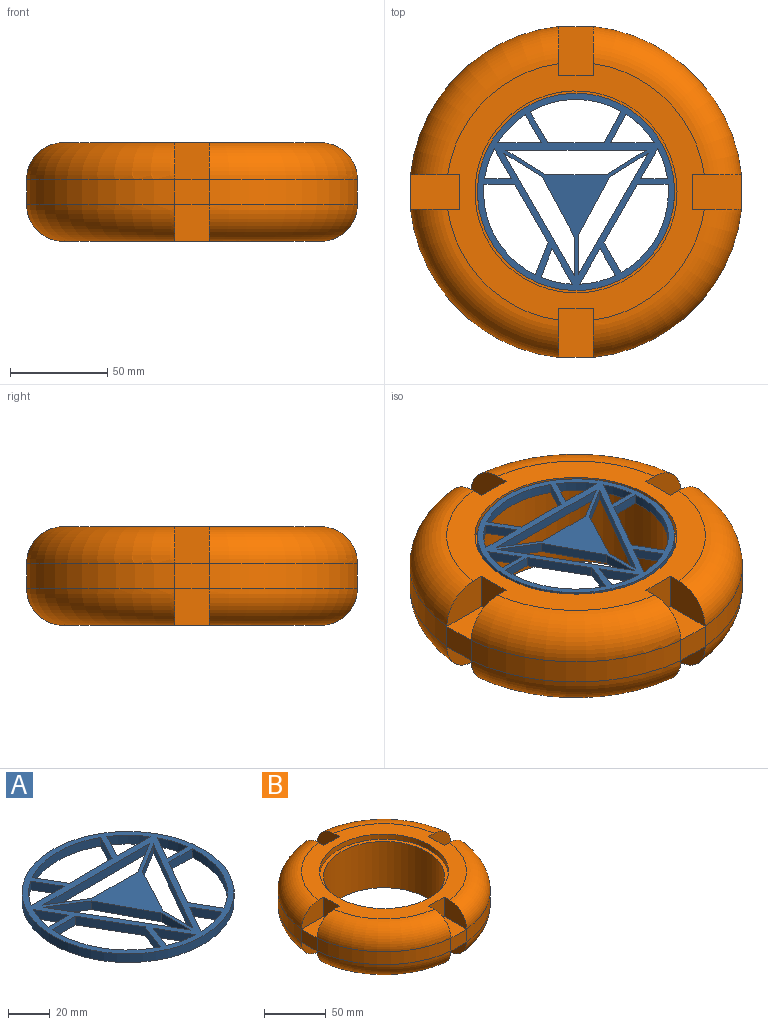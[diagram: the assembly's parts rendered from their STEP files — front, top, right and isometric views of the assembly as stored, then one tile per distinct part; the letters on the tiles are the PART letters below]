
ASSEMBLY  parts=2 mates=1
PART A: 45 faces, bbox 101.6x101.6x5.1 mm
  f0: plane 15.9x9.18mm, normal (0.87,0.5,0), area 93.3mm2, adj f1,f30,f43,f44
  f1: cylinder r=47.62mm len=46.89mm, axis (0,0,-1), area 249mm2, adj f0,f2,f43,f44
  f2: plane 16.2x8.64mm, normal (-0.88,0.47,0), area 93.3mm2, adj f1,f30,f43,f44
  f3: plane 22.36x5.08mm, normal (0,1,0), area 113.6mm2, adj f4,f31,f43,f44
  f4: plane 14.67x7.82mm, normal (0.88,-0.47,0), area 84.4mm2, adj f3,f31,f43,f44
  f5: plane 15.58x8.99mm, normal (0.87,0.5,0), area 91.4mm2, adj f6,f32,f43,f44
  f6: plane 29.95x17.29mm, normal (0.87,-0.5,0), area 175.7mm2, adj f5,f7,f43,f44
  f7: plane 15.8x5.08mm, normal (0,-1,0), area 80.3mm2, adj f6,f32,f43,f44
  f8: cylinder r=47.62mm len=16.12mm, axis (0,0,-1), area 84.2mm2, adj f9,f33,f43,f44
  f9: plane 14.79x5.57mm, normal (0.94,-0.35,0), area 80.3mm2, adj f8,f33,f43,f44
  f10: plane 30.93x16.49mm, normal (-0.88,-0.47,0), area 178mm2, adj f11,f34,f43,f44
  f11: plane 19.79x5.08mm, normal (-1,0,0), area 100.5mm2, adj f10,f12,f43,f44
  f12: plane 63.03x36.39mm, normal (0.87,0.5,0), area 369.7mm2, adj f11,f34,f43,f44
  f13: plane 30.31x16.16mm, normal (0.88,-0.47,0), area 174.5mm2, adj f14,f35,f43,f44
  f14: plane 19.9x12.32mm, normal (0.53,-0.85,0), area 118.9mm2, adj f13,f15,f43,f44
  f15: plane 62.46x36.06mm, normal (-0.87,0.5,0), area 366.4mm2, adj f14,f35,f43,f44
  f16: plane 31.25x5.08mm, normal (0,1,0), area 158.7mm2, adj f17,f36,f43,f44
  f17: plane 20.52x12.7mm, normal (0.53,0.85,0), area 122.6mm2, adj f16,f18,f43,f44
  f18: plane 72.28x5.08mm, normal (0,-1,0), area 367.2mm2, adj f17,f36,f43,f44
  f19: cylinder r=47.62mm len=14.36mm, axis (0,0,-1), area 102.9mm2, adj f20,f37,f43,f44
  f20: plane 14.36x8.29mm, normal (-0.87,-0.5,0), area 84.2mm2, adj f19,f37,f43,f44
  f21: cylinder r=47.62mm len=18.49mm, axis (0,0,-1), area 97.4mm2, adj f22,f38,f43,f44
  f22: plane 18.28x10.55mm, normal (0.87,-0.5,0), area 107.2mm2, adj f21,f38,f43,f44
  f23: cylinder r=47.62mm len=15.4mm, axis (0,0,-1), area 82.6mm2, adj f24,f39,f43,f44
  f24: plane 15.4x8.89mm, normal (-0.87,-0.5,0), area 90.3mm2, adj f23,f39,f43,f44
  f25: plane 29.95x17.29mm, normal (-0.87,-0.5,0), area 175.7mm2, adj f26,f40,f43,f44
  f26: plane 16.83x6.61mm, normal (-0.93,0.37,0), area 91.8mm2, adj f25,f27,f43,f44
  f27: cylinder r=47.62mm len=46.79mm, axis (0,0,-1), area 290.2mm2, adj f26,f40,f43,f44
  f28: plane 13.89x5.08mm, normal (0,1,0), area 70.6mm2, adj f29,f41,f43,f44
  f29: plane 15.4x8.89mm, normal (0.87,-0.5,0), area 90.3mm2, adj f28,f41,f43,f44
  f30: plane 29.07x5.08mm, normal (0,1,0), area 147.7mm2, adj f0,f2,f43,f44
  f31: cylinder r=47.62mm len=14.67mm, axis (0,0,-1), area 105.8mm2, adj f3,f4,f43,f44
  f32: cylinder r=47.62mm len=45.53mm, axis (0,0,-1), area 276.5mm2, adj f5,f7,f43,f44
  f33: plane 18.28x10.55mm, normal (-0.87,-0.5,0), area 107.2mm2, adj f8,f9,f43,f44
  f34: plane 19.9x12.32mm, normal (-0.53,-0.85,0), area 118.9mm2, adj f10,f12,f43,f44
  f35: plane 19.83x5.08mm, normal (1,0,0), area 100.7mm2, adj f13,f15,f43,f44
  f36: plane 20.52x12.7mm, normal (-0.53,0.85,0), area 122.6mm2, adj f16,f18,f43,f44
  f37: plane 22.36x5.08mm, normal (0,1,0), area 113.6mm2, adj f19,f20,f43,f44
  f38: plane 13.75x7.94mm, normal (-0.87,-0.5,0), area 80.6mm2, adj f21,f22,f43,f44
  f39: plane 13.89x5.08mm, normal (0,1,0), area 70.6mm2, adj f23,f24,f43,f44
  f40: plane 15.8x5.08mm, normal (0,-1,0), area 80.3mm2, adj f25,f27,f43,f44
  f41: cylinder r=47.62mm len=15.4mm, axis (0,0,-1), area 82.6mm2, adj f28,f29,f43,f44
  f42: cylinder r=50.8mm len=101.6mm, axis (0,0,-1), area 1621.5mm2, adj f43,f44
  f43: plane 101.6x101.6mm, normal (0,0,1), area 2830.3mm2, adj f0,f1,f2,f3,f4,f5,f6,f7
  f44: plane 101.6x101.6mm, normal (0,0,-1), area 2830.3mm2, adj f0,f1,f2,f3,f4,f5,f6,f7
PART B: 53 faces, bbox 184.6x184.6x50.8 mm
  f0: plane 25.4x19.05mm, normal (1,0,0), area 405.5mm2, adj f19,f30,f32,f49
  f1: plane 19.05x17.78mm, normal (0,-1,0), area 338.7mm2, adj f18,f20,f29,f50
  f2: plane 25.4x19.05mm, normal (-1,0,0), area 405.5mm2, adj f19,f30,f31,f49
  f3: plane 25.4x19.05mm, normal (0,-1,0), area 405.5mm2, adj f15,f30,f34,f46
  f4: plane 19.05x17.78mm, normal (-1,0,0), area 338.7mm2, adj f14,f16,f29,f47
  f5: plane 25.4x19.05mm, normal (0,1,0), area 405.5mm2, adj f15,f30,f32,f46
  f6: plane 25.4x19.05mm, normal (1,0,0), area 405.5mm2, adj f8,f30,f34,f43
  f7: plane 25.4x19.05mm, normal (-1,0,0), area 405.5mm2, adj f8,f30,f33,f43
  f8: plane 19.05x17.78mm, normal (0,1,0), area 338.7mm2, adj f6,f7,f30,f43
  f9: plane 25.4x19.05mm, normal (0,1,0), area 405.5mm2, adj f10,f30,f31,f40
  f10: plane 19.05x17.78mm, normal (1,0,0), area 338.7mm2, adj f9,f11,f30,f40
  f11: plane 25.4x19.05mm, normal (0,-1,0), area 405.5mm2, adj f10,f30,f33,f40
  f12: plane 25.4x19.05mm, normal (1,0,0), area 405.5mm2, adj f28,f29,f38,f44
  f13: cylinder r=85.72mm len=76.37mm, axis (0,0,-1), area 1483.9mm2, adj f34,f38,f42,f45
  f14: plane 25.4x19.05mm, normal (0,-1,0), area 405.5mm2, adj f4,f29,f38,f47
  f15: plane 19.05x17.78mm, normal (-1,0,0), area 338.7mm2, adj f3,f5,f30,f46
  f16: plane 25.4x19.05mm, normal (0,1,0), area 405.5mm2, adj f4,f29,f36,f47
  f17: cylinder r=85.72mm len=76.37mm, axis (0,0,-1), area 1483.9mm2, adj f32,f36,f45,f48
  f18: plane 25.4x19.05mm, normal (1,0,0), area 405.5mm2, adj f1,f29,f36,f50
  f19: plane 19.05x17.78mm, normal (0,-1,0), area 338.7mm2, adj f0,f2,f30,f49
  f20: plane 25.4x19.05mm, normal (-1,0,0), area 405.5mm2, adj f1,f29,f35,f50
  f21: cylinder r=85.72mm len=76.37mm, axis (0,0,-1), area 1483.9mm2, adj f31,f35,f39,f48
  f22: plane 25.4x19.05mm, normal (0,1,0), area 405.5mm2, adj f23,f29,f35,f41
  f23: plane 19.05x17.78mm, normal (1,0,0), area 338.7mm2, adj f22,f24,f29,f41
  f24: plane 25.4x19.05mm, normal (0,-1,0), area 405.5mm2, adj f23,f29,f37,f41
  f25: cylinder r=85.72mm len=76.37mm, axis (0,0,-1), area 1483.9mm2, adj f33,f37,f39,f42
  f26: plane 25.4x19.05mm, normal (-1,0,0), area 405.5mm2, adj f28,f29,f37,f44
  f27: cylinder r=52.07mm len=104.14mm, axis (0,0,-1), area 1662mm2, adj f29,f52
  f28: plane 19.05x17.78mm, normal (0,1,0), area 338.7mm2, adj f12,f26,f29,f44
  f29: plane 132.16x132.16mm, normal (0,0,1), area 4978mm2, adj f1,f4,f12,f14,f16,f18,f20,f22
  f30: plane 132.16x132.16mm, normal (0,0,-1), area 5985.1mm2, adj f0,f2,f3,f5,f6,f7,f8,f9
  f31: torus R=66.67mm, axis (0,0,1), area 3170.9mm2, adj f2,f9,f21,f30
  f32: torus R=66.67mm, axis (0,0,1), area 3170.9mm2, adj f0,f5,f17,f30
  f33: torus R=66.67mm, axis (0,0,1), area 3170.9mm2, adj f7,f11,f25,f30
  f34: torus R=66.67mm, axis (0,0,1), area 3170.9mm2, adj f3,f6,f13,f30
  f35: torus R=66.67mm, axis (0,0,1), area 3170.8mm2, adj f20,f21,f22,f29
  f36: torus R=66.67mm, axis (0,0,1), area 3170.8mm2, adj f16,f17,f18,f29
  f37: torus R=66.67mm, axis (0,0,1), area 3170.8mm2, adj f24,f25,f26,f29
  f38: torus R=66.67mm, axis (0,0,1), area 3170.8mm2, adj f12,f13,f14,f29
  f39: plane 17.78x12.7mm, normal (1,0,0), area 225.8mm2, adj f21,f25,f40,f41
  f40: plane 25.4x17.78mm, normal (0,0,-1), area 451.6mm2, adj f9,f10,f11,f39
  f41: plane 25.4x17.78mm, normal (0,0,1), area 451.6mm2, adj f22,f23,f24,f39
  f42: plane 17.78x12.7mm, normal (0,1,0), area 225.8mm2, adj f13,f25,f43,f44
  f43: plane 25.4x17.78mm, normal (0,0,-1), area 451.6mm2, adj f6,f7,f8,f42
  f44: plane 25.4x17.78mm, normal (0,0,1), area 451.6mm2, adj f12,f26,f28,f42
  f45: plane 17.78x12.7mm, normal (-1,0,0), area 225.8mm2, adj f13,f17,f46,f47
  f46: plane 25.4x17.78mm, normal (0,0,-1), area 451.6mm2, adj f3,f5,f15,f45
  f47: plane 25.4x17.78mm, normal (0,0,1), area 451.6mm2, adj f4,f14,f16,f45
  f48: plane 17.78x12.7mm, normal (0,-1,0), area 225.8mm2, adj f17,f21,f49,f50
  f49: plane 25.4x17.78mm, normal (0,0,-1), area 451.6mm2, adj f0,f2,f19,f48
  f50: plane 25.4x17.78mm, normal (0,0,1), area 451.6mm2, adj f1,f18,f20,f48
  f51: cylinder r=48.9mm len=97.79mm, axis (0,0,-1), area 14045.9mm2, adj f30,f52
  f52: plane 104.14x104.14mm, normal (0,0,1), area 1007.1mm2, adj f27,f51
PLACE A t=(19.29,14.37,25.17)mm
PLACE B t=(19.29,14.37,-20.55)mm
MATE slider A.f1 <-> B.f13  axis (0,0,1) through (19.29,14.37,30.25)mm
